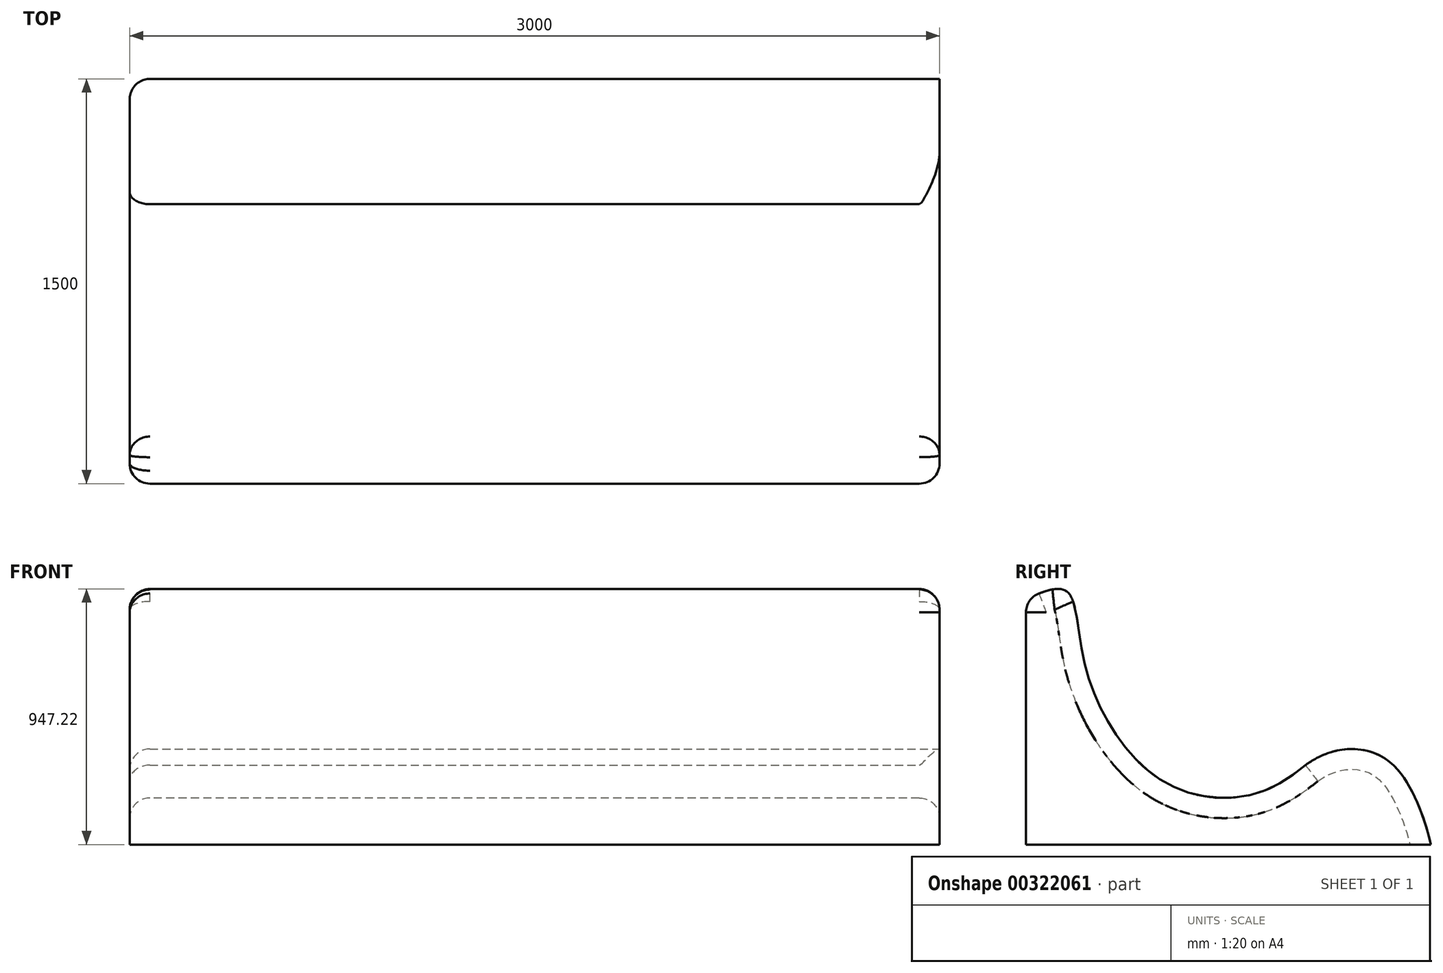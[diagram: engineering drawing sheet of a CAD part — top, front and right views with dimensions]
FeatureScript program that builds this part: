
annotation { "Feature Type Name" : "Feature", "Feature Type Description" : "" }
export const myFeature = defineFeature(function(context is Context, id is Id, definition is map)
    precondition{}
    {
        {
            var Q0;
            Q0=qCreatedBy(makeId("Top.planeOp"),FACE);
            var sketch = newSketch(context, id + "F0", { "sketchPlane" : qUnion([Q0])});
            skLineSegment(sketch, "E0.bottom", {"start": v(1500, 750) * mm, "end": v(-1500, 750) * mm});
            skLineSegment(sketch, "E0.top", {"start": v(1500, -750) * mm, "end": v(-1500, -750) * mm});
            skLineSegment(sketch, "E0.left", {"start": v(1500, 750) * mm, "end": v(1500, -750) * mm});
            skLineSegment(sketch, "E0.right", {"start": v(-1500, 750) * mm, "end": v(-1500, -750) * mm});
            skPoint(sketch, "E0.middle", {"position": v(0, 0) * mm});
            skSolve(sketch);
        }
        {
            var Q0;
            Q0=makeQuery(id+"F0.imprint","IMPRINT",FACE,{"disambiguationData":[TD([[makeQuery(id+"F0.imprint","IMPRINT",EDGE,{"derivedFrom":sQuery(id+"F0.wireOp",EDGE,"E0.bottom")}),1.0]])]});
            extrude(context, id + "F1", {"entities" : qUnion([Q0]), "depth" : 1100 * mm});
        }
        {
            var Q0;
            Q0=makeQuery(id+"F1.opExtrude","SWEPT_FACE",FACE,{"disambiguationData":[OSD([sQuery(id+"F0.wireOp",EDGE,"E0.left")])]});
            var sketch = newSketch(context, id + "F2", { "sketchPlane" : qUnion([Q0])});
            skFitSpline(sketch, "E1", {"points": [v(285.53, 294.34) * mm, v(72.43, 181.8) * mm, v(-258.57, 244.97) * mm, v(-531.42, 666.27) * mm, v(-600.03, 938.51) * mm, v(-750, 910.01) * mm], "startDerivative": vector(-1085.77, -869.27) * mm, "endDerivative": vector(-1225.47, -530.78) * mm});
            skFitSpline(sketch, "E2", {"points": [v(285.53, 294.34) * mm, v(562.47, 328.94) * mm, v(683.47, 189.49) * mm, v(750, 0) * mm], "startDerivative": vector(817.17, 592.14) * mm, "endDerivative": vector(134.38, -613.07) * mm});
            skSolve(sketch);
        }
        {
            var Q0;
            Q0 = qSketchRegion(id + "F2", true);
            var Q1;
            {var subQ2=sQuery(id+"F2.wireOp",EDGE,"E1");Q1=makeQuery(id+"F2.imprint","IMPRINT",FACE,{"disambiguationData":[TD([[makeQuery(id+"F2.imprint","IMPRINT",EDGE,{"derivedFrom":subQ2}),-1.0]])]});}
            extrude(context, id + "F3", {"entities" : qUnion([Q0, Q1]), "operationType" : NewBodyOperationType.REMOVE, "oppositeDirection" : true, "depth" : 3173 * mm});
        }
        {
            var Q0;
            Q0=makeQuery(id+"F3.boolean.opBoolean","INTERSECT",EDGE,{"derivedFrom":[makeQuery(id+"F1.opExtrude","SWEPT_FACE",FACE,{"disambiguationData":[OSD([sQuery(id+"F0.wireOp",EDGE,"E0.right")])]}),makeQuery(id+"F3.opExtrude","SWEPT_FACE",FACE,{"disambiguationData":[OSD([sQuery(id+"F2.wireOp",EDGE,"E2")])]})]});
            var Q1;
            Q1=makeQuery(id+"F3.boolean.opBoolean","INTERSECT",EDGE,{"derivedFrom":[makeQuery(id+"F1.opExtrude","SWEPT_FACE",FACE,{"disambiguationData":[OSD([sQuery(id+"F0.wireOp",EDGE,"E0.right")])]}),makeQuery(id+"F3.opExtrude","SWEPT_FACE",FACE,{"disambiguationData":[OSD([sQuery(id+"F2.wireOp",EDGE,"E1")])]})]});
            var Q2;
            Q2=makeQuery(id+"F3.boolean.opBoolean","COPY",EDGE,{"derivedFrom":makeQuery(id+"F3.opExtrude","SWEPT_EDGE",EDGE,{"disambiguationData":[OSD([sQuery(id+"F0.wireOp",EDGE,"E0.top"),sQuery(id+"F0.wireOp",EDGE,"E0.left"),sQuery(id+"F2.wireOp",EDGE,"E1")])]})});
            var Q3;
            Q3=makeQuery(id+"F1.opExtrude","SWEPT_EDGE",EDGE,{"disambiguationData":[OSD([sQuery(id+"F0.wireOp",EDGE,"E0.top"),sQuery(id+"F0.wireOp",EDGE,"E0.left")])]});
            var Q4;
            Q4=makeQuery(id+"F3.boolean.opBoolean","COPY",EDGE,{"derivedFrom":makeQuery(id+"F3.opExtrude","CAP_EDGE",EDGE,{"disambiguationData":[OSD([sQuery(id+"F2.wireOp",EDGE,"E1")])],"isStart":true})});
            var Q5;
            Q5=makeQuery(id+"F3.boolean.opBoolean","COPY",EDGE,{"derivedFrom":makeQuery(id+"F3.opExtrude","CAP_EDGE",EDGE,{"disambiguationData":[OSD([sQuery(id+"F2.wireOp",EDGE,"E2")])],"isStart":true})});
            fillet(context, id + "F4", {"entities" : qUnion([Q0, Q1, Q2, Q3, Q4, Q5]), "radius" : 75 * mm, "tangentPropagation" : true, "allowEdgeOverflow" : false});
        }
        {
            var Q0;
            Q0=makeQuery(id+"F1.opExtrude","SWEPT_EDGE",EDGE,{"disambiguationData":[OSD([sQuery(id+"F0.wireOp",EDGE,"E0.top"),sQuery(id+"F0.wireOp",EDGE,"E0.right")])]});
            fillet(context, id + "F5", {"entities" : qUnion([Q0]), "radius" : 75 * mm, "tangentPropagation" : true, "allowEdgeOverflow" : false});
        }
    });
